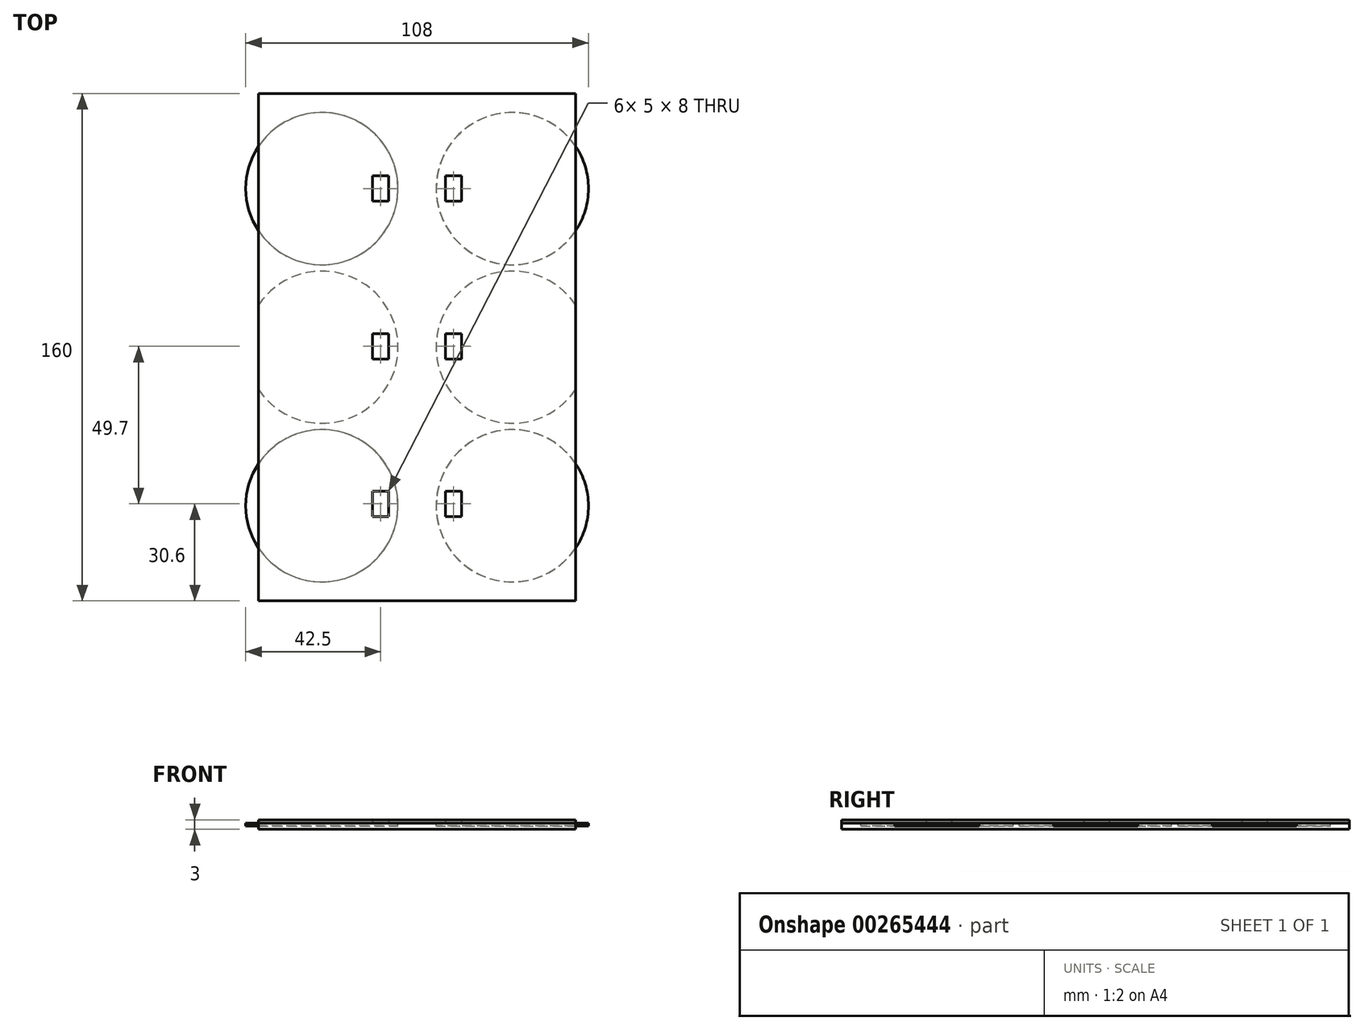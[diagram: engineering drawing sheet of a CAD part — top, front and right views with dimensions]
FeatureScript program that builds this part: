
annotation { "Feature Type Name" : "Feature", "Feature Type Description" : "" }
export const myFeature = defineFeature(function(context is Context, id is Id, definition is map)
    precondition{}
    {
        {
            var Q0;
            Q0=qCreatedBy(makeId("Top.planeOp"),FACE);
            var sketch = newSketch(context, id + "F0", { "sketchPlane" : qUnion([Q0])});
            skLineSegment(sketch, "E0.bottom", {"start": v(0, 0) * mm, "end": v(100, 0) * mm});
            skLineSegment(sketch, "E0.top", {"start": v(0, 160) * mm, "end": v(100, 160) * mm});
            skLineSegment(sketch, "E0.left", {"start": v(0, 0) * mm, "end": v(0, 160) * mm});
            skLineSegment(sketch, "E0.right", {"start": v(100, 0) * mm, "end": v(100, 160) * mm});
            skCircle(sketch, "E1", {"center": v(20, 130) * mm, "radius": 24 * mm});
            skCircle(sketch, "E2.0.1.0", {"center": v(20, 80) * mm, "radius": 24 * mm});
            skCircle(sketch, "E2.1.0.0", {"center": v(80, 130) * mm, "radius": 24 * mm});
            skCircle(sketch, "E2.1.1.0", {"center": v(80, 80) * mm, "radius": 24 * mm});
            skLineSegment(sketch, "E2.direction1", {"start": v(20, 130) * mm, "end": v(80, 130) * mm, "construction": true});
            skLineSegment(sketch, "E2.direction2", {"start": v(20, 130) * mm, "end": v(20, 80) * mm, "construction": true});
            skCircle(sketch, "E3.0.0.2", {"center": v(20, 30) * mm, "radius": 24 * mm});
            skCircle(sketch, "E3.0.1.2", {"center": v(80, 30) * mm, "radius": 24 * mm});
            skLineSegment(sketch, "E4.bottom", {"start": v(36, 134) * mm, "end": v(41, 134) * mm});
            skLineSegment(sketch, "E4.top", {"start": v(36, 126) * mm, "end": v(41, 126) * mm});
            skLineSegment(sketch, "E4.left", {"start": v(36, 134) * mm, "end": v(36, 126) * mm});
            skLineSegment(sketch, "E4.right", {"start": v(41, 134) * mm, "end": v(41, 126) * mm});
            skLineSegment(sketch, "E5.0.1.0", {"start": v(41, 84.3) * mm, "end": v(41, 76.3) * mm});
            skLineSegment(sketch, "E5.0.1.1", {"start": v(36, 84.3) * mm, "end": v(41, 84.3) * mm});
            skLineSegment(sketch, "E5.0.1.2", {"start": v(36, 84.3) * mm, "end": v(36, 76.3) * mm});
            skLineSegment(sketch, "E5.0.1.3", {"start": v(36, 76.3) * mm, "end": v(41, 76.3) * mm});
            skLineSegment(sketch, "E5.1.0.0", {"start": v(64, 134) * mm, "end": v(64, 126) * mm});
            skLineSegment(sketch, "E5.1.0.1", {"start": v(59, 134) * mm, "end": v(64, 134) * mm});
            skLineSegment(sketch, "E5.1.0.2", {"start": v(59, 134) * mm, "end": v(59, 126) * mm});
            skLineSegment(sketch, "E5.1.0.3", {"start": v(59, 126) * mm, "end": v(64, 126) * mm});
            skLineSegment(sketch, "E5.1.1.0", {"start": v(64, 84.3) * mm, "end": v(64, 76.3) * mm});
            skLineSegment(sketch, "E5.1.1.1", {"start": v(59, 84.3) * mm, "end": v(64, 84.3) * mm});
            skLineSegment(sketch, "E5.1.1.2", {"start": v(59, 84.3) * mm, "end": v(59, 76.3) * mm});
            skLineSegment(sketch, "E5.1.1.3", {"start": v(59, 76.3) * mm, "end": v(64, 76.3) * mm});
            skLineSegment(sketch, "E5.direction1", {"start": v(41, 126) * mm, "end": v(64, 126) * mm, "construction": true});
            skLineSegment(sketch, "E5.direction2", {"start": v(41, 126) * mm, "end": v(41, 76.3) * mm, "construction": true});
            skLineSegment(sketch, "E6.0.0.2", {"start": v(41, 34.6) * mm, "end": v(41, 26.6) * mm});
            skLineSegment(sketch, "E6.3.0.2", {"start": v(36, 34.6) * mm, "end": v(41, 34.6) * mm});
            skLineSegment(sketch, "E6.6.0.2", {"start": v(36, 34.6) * mm, "end": v(36, 26.6) * mm});
            skLineSegment(sketch, "E6.9.0.2", {"start": v(36, 26.6) * mm, "end": v(41, 26.6) * mm});
            skLineSegment(sketch, "E6.0.1.2", {"start": v(64, 34.6) * mm, "end": v(64, 26.6) * mm});
            skLineSegment(sketch, "E6.3.1.2", {"start": v(59, 34.6) * mm, "end": v(64, 34.6) * mm});
            skLineSegment(sketch, "E6.6.1.2", {"start": v(59, 34.6) * mm, "end": v(59, 26.6) * mm});
            skLineSegment(sketch, "E6.9.1.2", {"start": v(59, 26.6) * mm, "end": v(64, 26.6) * mm});
            skSolve(sketch);
        }
        {
            var Q0;
            Q0=makeQuery(id+"F0.imprint","IMPRINT",FACE,{"disambiguationData":[TD([[makeQuery(id+"F0.imprint","IMPRINT",EDGE,{"derivedFrom":sQuery(id+"F0.wireOp",EDGE,"E5.1.0.0")}),1.0]])]});
            var Q1;
            {var subQ16=sQuery(id+"F0.wireOp",EDGE,"E0.bottom");Q1=makeQuery(id+"F0.imprint","IMPRINT",FACE,{"disambiguationData":[TD([[makeQuery(id+"F0.imprint","IMPRINT",EDGE,{"derivedFrom":subQ16}),1.0]])]});}
            var Q2;
            Q2=makeQuery(id+"F0.imprint","IMPRINT",FACE,{"disambiguationData":[TD([[makeQuery(id+"F0.imprint","IMPRINT",EDGE,{"derivedFrom":sQuery(id+"F0.wireOp",EDGE,"E6.0.1.2")}),1.0]])]});
            var Q3;
            Q3=makeQuery(id+"F0.imprint","IMPRINT",FACE,{"disambiguationData":[TD([[makeQuery(id+"F0.imprint","IMPRINT",EDGE,{"derivedFrom":sQuery(id+"F0.wireOp",EDGE,"E5.0.1.0")}),1.0]])]});
            var Q4;
            Q4=makeQuery(id+"F0.imprint","IMPRINT",FACE,{"disambiguationData":[TD([[makeQuery(id+"F0.imprint","IMPRINT",EDGE,{"derivedFrom":sQuery(id+"F0.wireOp",EDGE,"E5.1.1.0")}),1.0]])]});
            var Q5;
            {var subQ0=sQuery(id+"F0.wireOp",EDGE,"E2.1.1.0");var subQ1=sQuery(id+"F0.wireOp",EDGE,"E0.right");var subQ2=makeQuery(id+"F0.imprint","INTERSECT",VERTEX,{"disambiguationData":[OD(1.0)],"derivedFrom":[subQ1,subQ0]});Q5=makeQuery(id+"F0.imprint","IMPRINT",FACE,{"disambiguationData":[TD([[makeQuery(id+"F0.imprint","IMPRINT",EDGE,{"disambiguationData":[TD([[subQ2,-1.0]])],"derivedFrom":subQ1}),1.0]])]});}
            var Q6;
            {var subQ0=sQuery(id+"F0.wireOp",EDGE,"E2.0.1.0");var subQ1=sQuery(id+"F0.wireOp",EDGE,"E0.left");var subQ2=makeQuery(id+"F0.imprint","INTERSECT",VERTEX,{"disambiguationData":[OD(1.0)],"derivedFrom":[subQ1,subQ0]});Q6=makeQuery(id+"F0.imprint","IMPRINT",FACE,{"disambiguationData":[TD([[makeQuery(id+"F0.imprint","IMPRINT",EDGE,{"disambiguationData":[TD([[subQ2,-1.0]])],"derivedFrom":subQ1}),-1.0]])]});}
            var Q7;
            {var subQ0=sQuery(id+"F0.wireOp",EDGE,"E3.0.1.2");var subQ1=sQuery(id+"F0.wireOp",EDGE,"E0.right");var subQ2=makeQuery(id+"F0.imprint","INTERSECT",VERTEX,{"disambiguationData":[OD(1.0)],"derivedFrom":[subQ1,subQ0]});Q7=makeQuery(id+"F0.imprint","IMPRINT",FACE,{"disambiguationData":[TD([[makeQuery(id+"F0.imprint","IMPRINT",EDGE,{"disambiguationData":[TD([[subQ2,-1.0]])],"derivedFrom":subQ1}),1.0]])]});}
            var Q8;
            Q8=makeQuery(id+"F0.imprint","IMPRINT",FACE,{"disambiguationData":[TD([[makeQuery(id+"F0.imprint","IMPRINT",EDGE,{"derivedFrom":sQuery(id+"F0.wireOp",EDGE,"E6.0.0.2")}),1.0]])]});
            var Q9;
            Q9=makeQuery(id+"F0.imprint","IMPRINT",FACE,{"disambiguationData":[TD([[makeQuery(id+"F0.imprint","IMPRINT",EDGE,{"derivedFrom":sQuery(id+"F0.wireOp",EDGE,"E4.bottom")}),1.0]])]});
            var Q10;
            Q10=makeQuery(id+"F0.imprint","IMPRINT",FACE,{"disambiguationData":[TD([[makeQuery(id+"F0.imprint","IMPRINT",EDGE,{"derivedFrom":sQuery(id+"F0.wireOp",EDGE,"E5.0.1.0")}),-1.0]])]});
            var Q11;
            Q11=makeQuery(id+"F0.imprint","IMPRINT",FACE,{"disambiguationData":[TD([[makeQuery(id+"F0.imprint","IMPRINT",EDGE,{"derivedFrom":sQuery(id+"F0.wireOp",EDGE,"E4.bottom")}),-1.0]])]});
            var Q12;
            Q12=makeQuery(id+"F0.imprint","IMPRINT",FACE,{"disambiguationData":[TD([[makeQuery(id+"F0.imprint","IMPRINT",EDGE,{"derivedFrom":sQuery(id+"F0.wireOp",EDGE,"E5.1.0.0")}),-1.0]])]});
            var Q13;
            Q13=makeQuery(id+"F0.imprint","IMPRINT",FACE,{"disambiguationData":[TD([[makeQuery(id+"F0.imprint","IMPRINT",EDGE,{"derivedFrom":sQuery(id+"F0.wireOp",EDGE,"E5.1.1.0")}),-1.0]])]});
            var Q14;
            Q14=makeQuery(id+"F0.imprint","IMPRINT",FACE,{"disambiguationData":[TD([[makeQuery(id+"F0.imprint","IMPRINT",EDGE,{"derivedFrom":sQuery(id+"F0.wireOp",EDGE,"E6.0.0.2")}),-1.0]])]});
            var Q15;
            Q15=makeQuery(id+"F0.imprint","IMPRINT",FACE,{"disambiguationData":[TD([[makeQuery(id+"F0.imprint","IMPRINT",EDGE,{"derivedFrom":sQuery(id+"F0.wireOp",EDGE,"E6.0.1.2")}),-1.0]])]});
            var Q16;
            {var subQ0=sQuery(id+"F0.wireOp",EDGE,"E3.0.0.2");var subQ1=sQuery(id+"F0.wireOp",EDGE,"E0.left");var subQ2=makeQuery(id+"F0.imprint","INTERSECT",VERTEX,{"disambiguationData":[OD(1.0)],"derivedFrom":[subQ1,subQ0]});Q16=makeQuery(id+"F0.imprint","IMPRINT",FACE,{"disambiguationData":[TD([[makeQuery(id+"F0.imprint","IMPRINT",EDGE,{"disambiguationData":[TD([[subQ2,-1.0]])],"derivedFrom":subQ1}),-1.0]])]});}
            extrude(context, id + "F1", {"entities" : qUnion([Q0, Q1, Q2, Q3, Q4, Q5, Q6, Q7, Q8, Q9, Q10, Q11, Q12, Q13, Q14, Q15, Q16]), "oppositeDirection" : true, "depth" : 2 * mm});
        }
        {
            var Q0;
            Q0=makeQuery(id+"F0.imprint","IMPRINT",FACE,{"disambiguationData":[TD([[makeQuery(id+"F0.imprint","IMPRINT",EDGE,{"derivedFrom":sQuery(id+"F0.wireOp",EDGE,"E4.bottom")}),1.0]])]});
            var Q1;
            Q1=makeQuery(id+"F0.imprint","IMPRINT",FACE,{"disambiguationData":[TD([[makeQuery(id+"F0.imprint","IMPRINT",EDGE,{"derivedFrom":sQuery(id+"F0.wireOp",EDGE,"E4.bottom")}),-1.0]])]});
            var Q2;
            Q2=makeQuery(id+"F0.imprint","IMPRINT",FACE,{"disambiguationData":[TD([[makeQuery(id+"F0.imprint","IMPRINT",EDGE,{"derivedFrom":sQuery(id+"F0.wireOp",EDGE,"E5.1.0.0")}),1.0]])]});
            var Q3;
            Q3=makeQuery(id+"F0.imprint","IMPRINT",FACE,{"disambiguationData":[TD([[makeQuery(id+"F0.imprint","IMPRINT",EDGE,{"derivedFrom":sQuery(id+"F0.wireOp",EDGE,"E5.1.0.0")}),-1.0]])]});
            var Q4;
            Q4=makeQuery(id+"F0.imprint","IMPRINT",FACE,{"disambiguationData":[TD([[makeQuery(id+"F0.imprint","IMPRINT",EDGE,{"derivedFrom":sQuery(id+"F0.wireOp",EDGE,"E5.0.1.0")}),1.0]])]});
            var Q5;
            Q5=makeQuery(id+"F0.imprint","IMPRINT",FACE,{"disambiguationData":[TD([[makeQuery(id+"F0.imprint","IMPRINT",EDGE,{"derivedFrom":sQuery(id+"F0.wireOp",EDGE,"E5.0.1.0")}),-1.0]])]});
            var Q6;
            Q6=makeQuery(id+"F0.imprint","IMPRINT",FACE,{"disambiguationData":[TD([[makeQuery(id+"F0.imprint","IMPRINT",EDGE,{"derivedFrom":sQuery(id+"F0.wireOp",EDGE,"E5.1.1.0")}),1.0]])]});
            var Q7;
            Q7=makeQuery(id+"F0.imprint","IMPRINT",FACE,{"disambiguationData":[TD([[makeQuery(id+"F0.imprint","IMPRINT",EDGE,{"derivedFrom":sQuery(id+"F0.wireOp",EDGE,"E5.1.1.0")}),-1.0]])]});
            var Q8;
            Q8=makeQuery(id+"F0.imprint","IMPRINT",FACE,{"disambiguationData":[TD([[makeQuery(id+"F0.imprint","IMPRINT",EDGE,{"derivedFrom":sQuery(id+"F0.wireOp",EDGE,"E6.0.0.2")}),1.0]])]});
            var Q9;
            Q9=makeQuery(id+"F0.imprint","IMPRINT",FACE,{"disambiguationData":[TD([[makeQuery(id+"F0.imprint","IMPRINT",EDGE,{"derivedFrom":sQuery(id+"F0.wireOp",EDGE,"E6.0.1.2")}),1.0]])]});
            var Q10;
            Q10=makeQuery(id+"F0.imprint","IMPRINT",FACE,{"disambiguationData":[TD([[makeQuery(id+"F0.imprint","IMPRINT",EDGE,{"derivedFrom":sQuery(id+"F0.wireOp",EDGE,"E6.0.0.2")}),-1.0]])]});
            var Q11;
            Q11=makeQuery(id+"F0.imprint","IMPRINT",FACE,{"disambiguationData":[TD([[makeQuery(id+"F0.imprint","IMPRINT",EDGE,{"derivedFrom":sQuery(id+"F0.wireOp",EDGE,"E6.0.1.2")}),-1.0]])]});
            extrude(context, id + "F2", {"entities" : qUnion([Q0, Q1, Q2, Q3, Q4, Q5, Q6, Q7, Q8, Q9, Q10, Q11]), "operationType" : NewBodyOperationType.REMOVE, "oppositeDirection" : true, "depth" : 1 * mm});
        }
        {
            var Q0;
            Q0=makeQuery(id+"F0.imprint","IMPRINT",FACE,{"disambiguationData":[TD([[makeQuery(id+"F0.imprint","IMPRINT",EDGE,{"derivedFrom":sQuery(id+"F0.wireOp",EDGE,"E4.bottom")}),1.0]])]});
            var Q1;
            {var subQ0=sQuery(id+"F0.wireOp",EDGE,"E1");var subQ1=sQuery(id+"F0.wireOp",EDGE,"E0.left");var subQ2=makeQuery(id+"F0.imprint","INTERSECT",VERTEX,{"disambiguationData":[OD(0.0)],"derivedFrom":[subQ1,subQ0]});Q1=makeQuery(id+"F0.imprint","IMPRINT",FACE,{"disambiguationData":[TD([[makeQuery(id+"F0.imprint","IMPRINT",EDGE,{"disambiguationData":[TD([[subQ2,-1.0]])],"derivedFrom":subQ1}),1.0]])]});}
            var Q2;
            Q2=makeQuery(id+"F0.imprint","IMPRINT",FACE,{"disambiguationData":[TD([[makeQuery(id+"F0.imprint","IMPRINT",EDGE,{"derivedFrom":sQuery(id+"F0.wireOp",EDGE,"E5.1.0.0")}),1.0]])]});
            var Q3;
            {var subQ0=sQuery(id+"F0.wireOp",EDGE,"E2.1.0.0");var subQ1=sQuery(id+"F0.wireOp",EDGE,"E0.right");var subQ2=makeQuery(id+"F0.imprint","INTERSECT",VERTEX,{"disambiguationData":[OD(0.0)],"derivedFrom":[subQ1,subQ0]});Q3=makeQuery(id+"F0.imprint","IMPRINT",FACE,{"disambiguationData":[TD([[makeQuery(id+"F0.imprint","IMPRINT",EDGE,{"disambiguationData":[TD([[subQ2,-1.0]])],"derivedFrom":subQ1}),-1.0]])]});}
            var Q4;
            {var subQ0=sQuery(id+"F0.wireOp",EDGE,"E2.1.1.0");var subQ1=sQuery(id+"F0.wireOp",EDGE,"E0.right");var subQ2=makeQuery(id+"F0.imprint","INTERSECT",VERTEX,{"disambiguationData":[OD(0.0)],"derivedFrom":[subQ1,subQ0]});Q4=makeQuery(id+"F0.imprint","IMPRINT",FACE,{"disambiguationData":[TD([[makeQuery(id+"F0.imprint","IMPRINT",EDGE,{"disambiguationData":[TD([[subQ2,-1.0]])],"derivedFrom":subQ1}),-1.0]])]});}
            var Q5;
            Q5=makeQuery(id+"F0.imprint","IMPRINT",FACE,{"disambiguationData":[TD([[makeQuery(id+"F0.imprint","IMPRINT",EDGE,{"derivedFrom":sQuery(id+"F0.wireOp",EDGE,"E6.0.1.2")}),1.0]])]});
            var Q6;
            {var subQ0=sQuery(id+"F0.wireOp",EDGE,"E3.0.1.2");var subQ1=sQuery(id+"F0.wireOp",EDGE,"E0.right");var subQ2=makeQuery(id+"F0.imprint","INTERSECT",VERTEX,{"disambiguationData":[OD(0.0)],"derivedFrom":[subQ1,subQ0]});Q6=makeQuery(id+"F0.imprint","IMPRINT",FACE,{"disambiguationData":[TD([[makeQuery(id+"F0.imprint","IMPRINT",EDGE,{"disambiguationData":[TD([[subQ2,-1.0]])],"derivedFrom":subQ1}),-1.0]])]});}
            var Q7;
            Q7=makeQuery(id+"F0.imprint","IMPRINT",FACE,{"disambiguationData":[TD([[makeQuery(id+"F0.imprint","IMPRINT",EDGE,{"derivedFrom":sQuery(id+"F0.wireOp",EDGE,"E6.0.0.2")}),1.0]])]});
            var Q8;
            {var subQ0=sQuery(id+"F0.wireOp",EDGE,"E3.0.0.2");var subQ1=sQuery(id+"F0.wireOp",EDGE,"E0.left");var subQ2=makeQuery(id+"F0.imprint","INTERSECT",VERTEX,{"disambiguationData":[OD(0.0)],"derivedFrom":[subQ1,subQ0]});Q8=makeQuery(id+"F0.imprint","IMPRINT",FACE,{"disambiguationData":[TD([[makeQuery(id+"F0.imprint","IMPRINT",EDGE,{"disambiguationData":[TD([[subQ2,-1.0]])],"derivedFrom":subQ1}),1.0]])]});}
            var Q9;
            {var subQ0=sQuery(id+"F0.wireOp",EDGE,"E2.0.1.0");var subQ1=sQuery(id+"F0.wireOp",EDGE,"E0.left");var subQ2=makeQuery(id+"F0.imprint","INTERSECT",VERTEX,{"disambiguationData":[OD(0.0)],"derivedFrom":[subQ1,subQ0]});Q9=makeQuery(id+"F0.imprint","IMPRINT",FACE,{"disambiguationData":[TD([[makeQuery(id+"F0.imprint","IMPRINT",EDGE,{"disambiguationData":[TD([[subQ2,-1.0]])],"derivedFrom":subQ1}),1.0]])]});}
            var Q10;
            Q10=makeQuery(id+"F0.imprint","IMPRINT",FACE,{"disambiguationData":[TD([[makeQuery(id+"F0.imprint","IMPRINT",EDGE,{"derivedFrom":sQuery(id+"F0.wireOp",EDGE,"E5.0.1.0")}),1.0]])]});
            var Q11;
            Q11=makeQuery(id+"F0.imprint","IMPRINT",FACE,{"disambiguationData":[TD([[makeQuery(id+"F0.imprint","IMPRINT",EDGE,{"derivedFrom":sQuery(id+"F0.wireOp",EDGE,"E4.bottom")}),-1.0]])]});
            var Q12;
            Q12=makeQuery(id+"F0.imprint","IMPRINT",FACE,{"disambiguationData":[TD([[makeQuery(id+"F0.imprint","IMPRINT",EDGE,{"derivedFrom":sQuery(id+"F0.wireOp",EDGE,"E5.1.0.0")}),-1.0]])]});
            var Q13;
            Q13=makeQuery(id+"F0.imprint","IMPRINT",FACE,{"disambiguationData":[TD([[makeQuery(id+"F0.imprint","IMPRINT",EDGE,{"derivedFrom":sQuery(id+"F0.wireOp",EDGE,"E5.0.1.0")}),-1.0]])]});
            var Q14;
            Q14=makeQuery(id+"F0.imprint","IMPRINT",FACE,{"disambiguationData":[TD([[makeQuery(id+"F0.imprint","IMPRINT",EDGE,{"derivedFrom":sQuery(id+"F0.wireOp",EDGE,"E6.0.0.2")}),-1.0]])]});
            var Q15;
            Q15=makeQuery(id+"F0.imprint","IMPRINT",FACE,{"disambiguationData":[TD([[makeQuery(id+"F0.imprint","IMPRINT",EDGE,{"derivedFrom":sQuery(id+"F0.wireOp",EDGE,"E6.0.1.2")}),-1.0]])]});
            extrude(context, id + "F3", {"entities" : qUnion([Q0, Q1, Q2, Q3, Q4, Q5, Q6, Q7, Q8, Q9, Q10, Q11, Q12, Q13, Q14, Q15]), "oppositeDirection" : true, "depth" : 1 * mm});
        }
        {
            var Q0;
            {var subQ16=sQuery(id+"F0.wireOp",EDGE,"E0.bottom");Q0=makeQuery(id+"F0.imprint","IMPRINT",FACE,{"disambiguationData":[TD([[makeQuery(id+"F0.imprint","IMPRINT",EDGE,{"derivedFrom":subQ16}),1.0]])]});}
            var Q1;
            Q1=makeQuery(id+"F0.imprint","IMPRINT",FACE,{"disambiguationData":[TD([[makeQuery(id+"F0.imprint","IMPRINT",EDGE,{"derivedFrom":sQuery(id+"F0.wireOp",EDGE,"E4.bottom")}),1.0]])]});
            var Q2;
            Q2=makeQuery(id+"F0.imprint","IMPRINT",FACE,{"disambiguationData":[TD([[makeQuery(id+"F0.imprint","IMPRINT",EDGE,{"derivedFrom":sQuery(id+"F0.wireOp",EDGE,"E5.1.0.0")}),1.0]])]});
            var Q3;
            Q3=makeQuery(id+"F0.imprint","IMPRINT",FACE,{"disambiguationData":[TD([[makeQuery(id+"F0.imprint","IMPRINT",EDGE,{"derivedFrom":sQuery(id+"F0.wireOp",EDGE,"E5.1.1.0")}),1.0]])]});
            var Q4;
            Q4=makeQuery(id+"F0.imprint","IMPRINT",FACE,{"disambiguationData":[TD([[makeQuery(id+"F0.imprint","IMPRINT",EDGE,{"derivedFrom":sQuery(id+"F0.wireOp",EDGE,"E5.0.1.0")}),1.0]])]});
            var Q5;
            Q5=makeQuery(id+"F0.imprint","IMPRINT",FACE,{"disambiguationData":[TD([[makeQuery(id+"F0.imprint","IMPRINT",EDGE,{"derivedFrom":sQuery(id+"F0.wireOp",EDGE,"E6.0.0.2")}),1.0]])]});
            var Q6;
            Q6=makeQuery(id+"F0.imprint","IMPRINT",FACE,{"disambiguationData":[TD([[makeQuery(id+"F0.imprint","IMPRINT",EDGE,{"derivedFrom":sQuery(id+"F0.wireOp",EDGE,"E6.0.1.2")}),1.0]])]});
            extrude(context, id + "F4", {"entities" : qUnion([Q0, Q1, Q2, Q3, Q4, Q5, Q6]), "depth" : 1 * mm});
        }
    });
